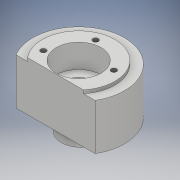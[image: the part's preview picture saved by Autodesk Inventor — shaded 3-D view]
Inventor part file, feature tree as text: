
AUTODESK INVENTOR PART (.ipt)
format: ipt  version: 2018 (Build 220112000, 112)  size: 146,944 bytes
history: native  units: mm
features: sketch x7, extrude x6, reference x3, hole x1
ambient origin geometry x8: Origin, YZ Plane, XZ Plane, XY Plane, X Axis, Y Axis, Z Axis, Center Point
bodies: Solid1 (feature_tree)
feature tree (17):
  extrude  "Extrusion1"  Depth=35.0mm TaperAngle=0.0deg
  extrude  "Extrusion2"  Depth=2.5mm TaperAngle=0.0deg
  extrude  "Extrusion3"  Depth=18.0mm TaperAngle=0.0deg
  extrude  "Extrusion4"  Depth=18.0mm TaperAngle=0.0deg
  extrude  "Extrusion5"  Depth=3.3mm
  extrude  "Extrusion6"  Depth=10.0mm TaperAngle=0.0deg
  hole  "Hole1"  [1 undecoded]
  sketch  "Sketch1"  dims[d0=69.5mm d1=35.0mm d2=0.0mm]
  sketch  "Sketch2"  dims[d3=55.0mm d4=2.5mm d5=0.0mm]
  sketch  "Sketch3"  dims[d6=34.0mm d7=18.0mm d8=0.0mm]
  sketch  "Sketch4"  dims[d9=19.7mm d10=18.0mm d11=0.0mm]
  sketch  "Sketch5"  dims[d12=30.0mm d13=3.3mm]
  sketch  "Sketch6"  dims[d14=7.0mm d15=10.0mm d16=0.0mm]
  sketch  "Sketch7"  dims[d17=52.3mm d18=10.0mm d19=0.0mm d20=4.134mm d21=10.0mm d22=4.0mm d23=2.0mm d24=90.0deg d25=14.2mm d26=20.594885mm]
  reference  "Reference1"
  reference  "Reference2"
  reference  "Reference3"
note: 1 required parameter value undecoded (feature->parameter linkage not recoverable at this tier; creation-order binding heuristic only, values carry confidence <= 0.55)
